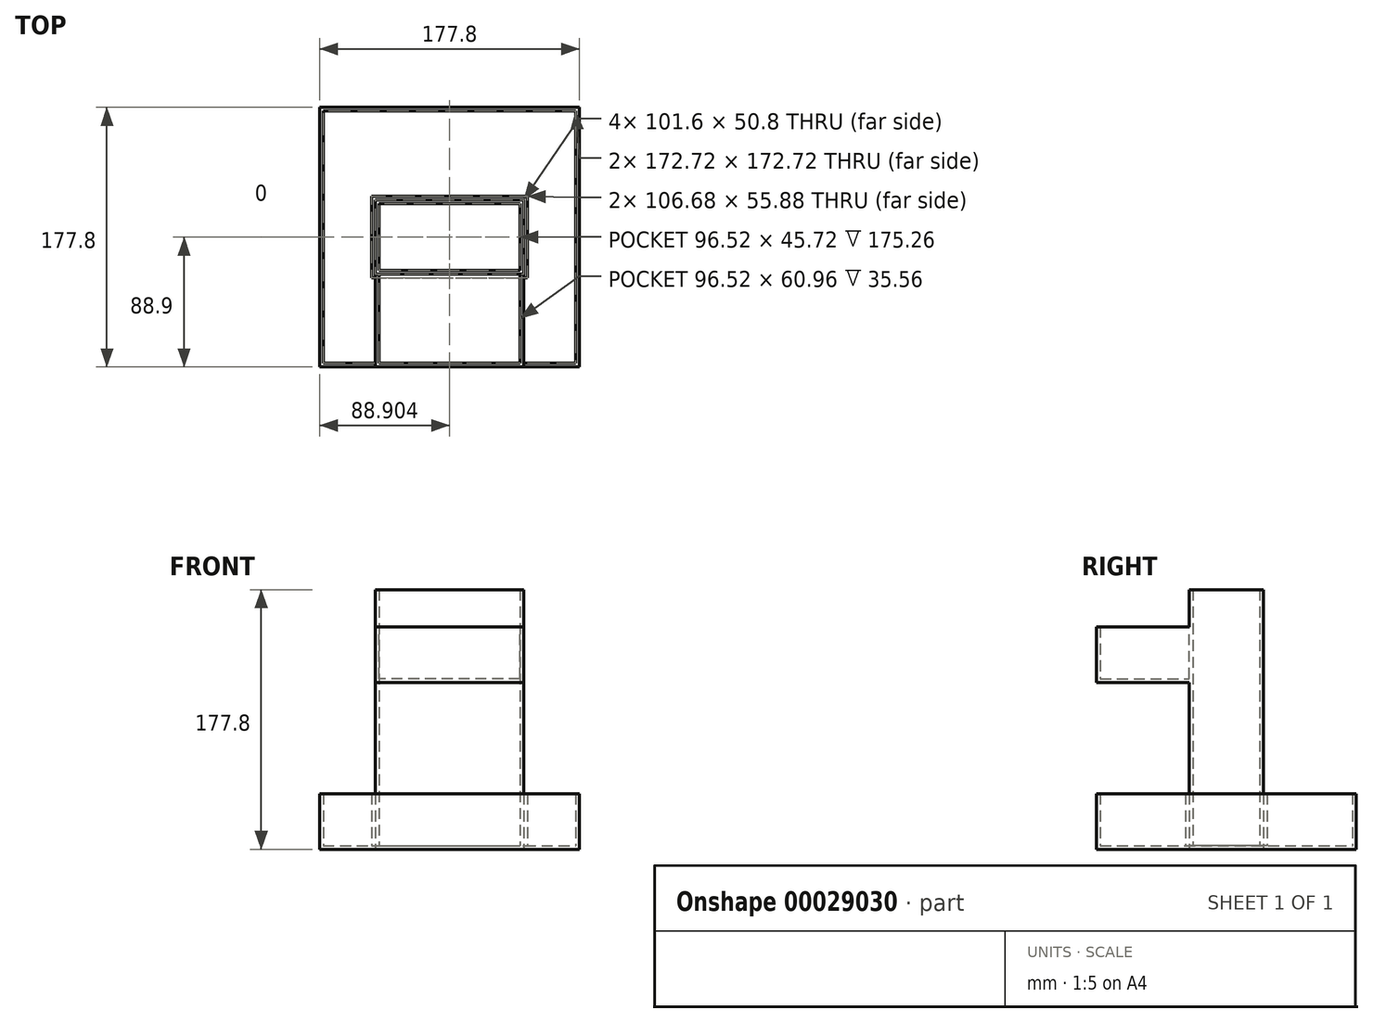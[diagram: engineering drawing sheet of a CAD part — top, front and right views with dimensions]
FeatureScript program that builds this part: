
annotation { "Feature Type Name" : "Feature", "Feature Type Description" : "" }
export const myFeature = defineFeature(function(context is Context, id is Id, definition is map)
    precondition{}
    {
        {
            var Q0;
            Q0=qCreatedBy(makeId("Front.planeOp"),FACE);
            var sketch = newSketch(context, id + "F0", { "sketchPlane" : qUnion([Q0])});
            skLineSegment(sketch, "E0.bottom", {"start": v(-40.73, 111.85) * mm, "end": v(60.87, 111.85) * mm});
            skLineSegment(sketch, "E0.top", {"start": v(-40.73, -65.95) * mm, "end": v(60.87, -65.95) * mm});
            skLineSegment(sketch, "E0.left", {"start": v(-40.73, 111.85) * mm, "end": v(-40.73, -65.95) * mm});
            skLineSegment(sketch, "E0.right", {"start": v(60.87, 111.85) * mm, "end": v(60.87, -65.95) * mm});
            skSolve(sketch);
        }
        {
            var Q0;
            Q0=makeQuery(id+"F0.imprint","IMPRINT",FACE,{"disambiguationData":[TD([[makeQuery(id+"F0.imprint","IMPRINT",EDGE,{"derivedFrom":sQuery(id+"F0.wireOp",EDGE,"E0.bottom")}),-1.0]])]});
            extrude(context, id + "F1", {"entities" : qUnion([Q0]), "oppositeDirection" : true, "depth" : 50.8 * mm});
        }
        {
            var Q0;
            Q0=makeQuery(id+"F1.opExtrude","SWEPT_FACE",FACE,{"disambiguationData":[OSD([sQuery(id+"F0.wireOp",EDGE,"E0.bottom")])]});
            shell(context, id + "F2", {"entities" : qUnion([Q0]), "thickness" : 2.54 * mm});
        }
        {
            var Q0;
            Q0=makeQuery(id+"F1.opExtrude","SWEPT_FACE",FACE,{"disambiguationData":[OSD([sQuery(id+"F0.wireOp",EDGE,"E0.top")])]});
            var sketch = newSketch(context, id + "F3", { "sketchPlane" : qUnion([Q0])});
            skLineSegment(sketch, "E1.bottom", {"start": v(-78.83, 63.5) * mm, "end": v(98.97, 63.5) * mm});
            skLineSegment(sketch, "E1.top", {"start": v(-78.83, -114.3) * mm, "end": v(98.97, -114.3) * mm});
            skLineSegment(sketch, "E1.left", {"start": v(-78.83, 63.5) * mm, "end": v(-78.83, -114.3) * mm});
            skLineSegment(sketch, "E1.right", {"start": v(98.97, 63.5) * mm, "end": v(98.97, -114.3) * mm});
            skSolve(sketch);
        }
        {
            var Q0;
            Q0=makeQuery(id+"F3.imprint","IMPRINT",FACE,{"disambiguationData":[TD([[makeQuery(id+"F3.imprint","IMPRINT",EDGE,{"derivedFrom":sQuery(id+"F3.wireOp",EDGE,"E1.bottom")}),-1.0]])]});
            extrude(context, id + "F4", {"entities" : qUnion([Q0]), "oppositeDirection" : true, "depth" : 38.1 * mm});
        }
        {
            var Q0;
            Q0=makeQuery(id+"F4.opExtrude","CAP_FACE",FACE,{"disambiguationData":[OSD([sQuery(id+"F0.wireOp",EDGE,"E0.top"),sQuery(id+"F0.wireOp",EDGE,"E0.left"),sQuery(id+"F0.wireOp",EDGE,"E0.right"),sQuery(id+"F3.wireOp",EDGE,"E1.bottom"),sQuery(id+"F3.wireOp",EDGE,"E1.top"),sQuery(id+"F3.wireOp",EDGE,"E1.left"),sQuery(id+"F3.wireOp",EDGE,"E1.right")])],"isStart":false});
            shell(context, id + "F5", {"entities" : qUnion([Q0]), "thickness" : 2.54 * mm});
        }
        {
            var Q0;
            Q0=makeQuery(id+"F1.opExtrude","CAP_FACE",FACE,{"disambiguationData":[OSD([sQuery(id+"F0.wireOp",EDGE,"E0.bottom"),sQuery(id+"F0.wireOp",EDGE,"E0.top"),sQuery(id+"F0.wireOp",EDGE,"E0.left"),sQuery(id+"F0.wireOp",EDGE,"E0.right")])],"isStart":true});
            var sketch = newSketch(context, id + "F6", { "sketchPlane" : qUnion([Q0])});
            skLineSegment(sketch, "E2.bottom", {"start": v(-40.73, 86.45) * mm, "end": v(60.87, 86.45) * mm});
            skLineSegment(sketch, "E2.top", {"start": v(-40.73, 48.35) * mm, "end": v(60.87, 48.35) * mm});
            skLineSegment(sketch, "E2.left", {"start": v(-40.73, 86.45) * mm, "end": v(-40.73, 48.35) * mm});
            skLineSegment(sketch, "E2.right", {"start": v(60.87, 86.45) * mm, "end": v(60.87, 48.35) * mm});
            skSolve(sketch);
        }
        {
            var Q0;
            Q0=makeQuery(id+"F6.imprint","IMPRINT",FACE,{"disambiguationData":[TD([[makeQuery(id+"F6.imprint","IMPRINT",EDGE,{"derivedFrom":sQuery(id+"F6.wireOp",EDGE,"E2.bottom")}),-1.0]])]});
            extrude(context, id + "F7", {"entities" : qUnion([Q0]), "operationType" : NewBodyOperationType.ADD, "depth" : 63.5 * mm});
        }
        {
            var Q0;
            Q0=makeQuery(id+"F7.opExtrude","SWEPT_FACE",FACE,{"disambiguationData":[OSD([sQuery(id+"F6.wireOp",EDGE,"E2.bottom")])]});
            shell(context, id + "F8", {"entities" : qUnion([Q0]), "thickness" : 2.54 * mm});
        }
    });
